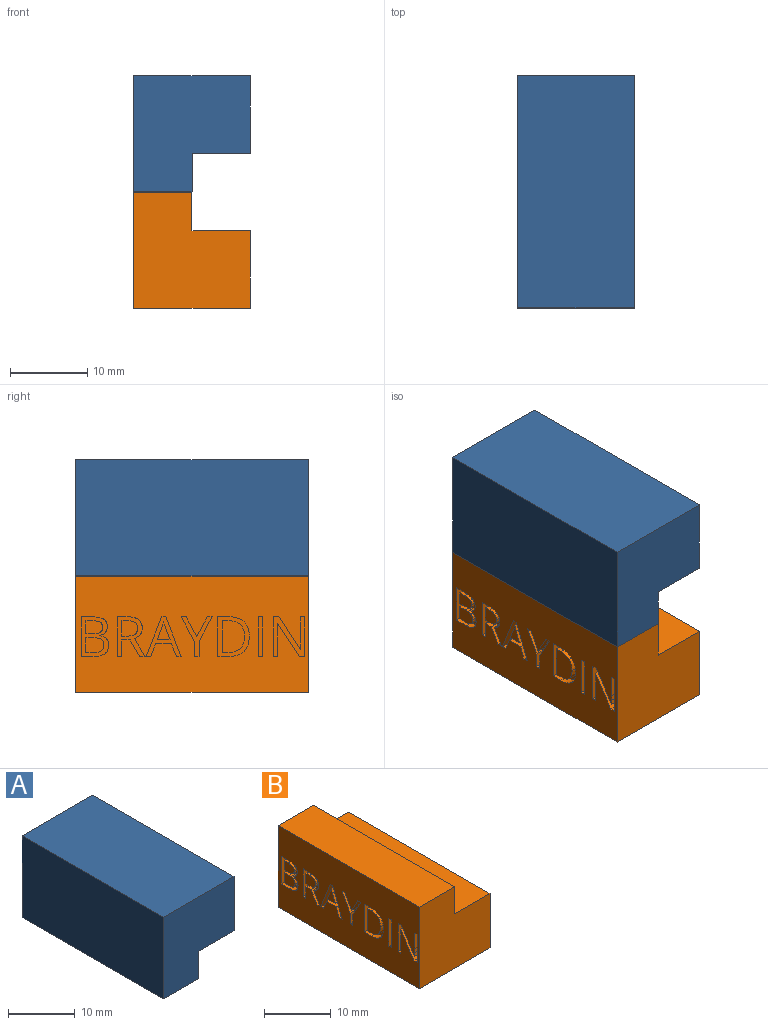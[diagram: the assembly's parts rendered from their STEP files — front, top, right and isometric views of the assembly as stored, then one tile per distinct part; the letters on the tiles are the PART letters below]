
ASSEMBLY  parts=2 mates=1
PART A: 8 faces, bbox 15x30x15 mm
  f0: plane 30x15mm, normal (0,0,1), area 450mm2, adj f1,f2,f3,f6
  f1: plane 30x15mm, normal (-1,0,0), area 450mm2, adj f0,f2,f3,f5
  f2: plane 15x15mm, normal (0,-1,0), area 187.5mm2, adj f0,f1,f4,f5,f6,f7
  f3: plane 15x15mm, normal (0,1,0), area 187.5mm2, adj f0,f1,f4,f5,f6,f7
  f4: plane 30x5mm, normal (1,0,0), area 150mm2, adj f2,f3,f5,f7
  f5: plane 30x7.5mm, normal (0,0,-1), area 225mm2, adj f1,f2,f3,f4
  f6: plane 30x10mm, normal (1,0,0), area 300mm2, adj f0,f2,f3,f7
  f7: plane 30x7.5mm, normal (0,0,-1), area 225mm2, adj f2,f3,f4,f6
PART B: 118 faces, bbox 15x30x15 mm
  f0: plane 30x15mm, normal (-1,0,0), area 378.6mm2, adj f1,f3,f4,f7,f8,f9,f10,f11
  f1: plane 15x15mm, normal (0,-1,0), area 187.5mm2, adj f0,f2,f4,f5,f6,f7
  f2: plane 30x5mm, normal (1,0,0), area 150mm2, adj f1,f3,f6,f7
  f3: plane 15x15mm, normal (0,1,0), area 187.5mm2, adj f0,f2,f4,f5,f6,f7
  f4: plane 30x15mm, normal (0,0,-1), area 450mm2, adj f0,f1,f3,f5
  f5: plane 30x10mm, normal (1,0,0), area 300mm2, adj f1,f3,f4,f6
  f6: plane 30x7.5mm, normal (0,0,1), area 225mm2, adj f1,f2,f3,f5
  f7: plane 30x7.5mm, normal (0,0,1), area 225mm2, adj f0,f1,f2,f3
  f8: plane 2.56x1.36mm, normal (0,-0.88,-0.47), area 2.9mm2, adj f0,f9,f16,f17
  f9: plane 2.56x1.35mm, normal (0,0.88,-0.47), area 2.9mm2, adj f0,f8,f10,f17
  f10: plane 1x0.65mm, normal (0,0,-1), area 0.7mm2, adj f0,f9,f11,f17
  f11: plane 3.16x1.7mm, normal (0,-0.88,0.47), area 3.6mm2, adj f0,f10,f12,f17
  f12: plane 1.96x1mm, normal (0,-1,0), area 2mm2, adj f0,f11,f13,f17
  f13: plane 1x0.6mm, normal (0,0,1), area 0.6mm2, adj f0,f12,f14,f17
  f14: plane 1.98x1mm, normal (0,1,0), area 2mm2, adj f0,f13,f15,f17
  f15: plane 3.13x1.71mm, normal (0,0.88,0.48), area 3.6mm2, adj f0,f14,f16,f17
  f16: plane 1x0.64mm, normal (0,0,-1), area 0.6mm2, adj f0,f8,f15,f17
  f17: plane 5.11x4.01mm, normal (-1,0,0), area 5mm2, adj f8,f9,f10,f11,f12,f13,f14,f15
  f18: plane 1.91x1mm, normal (0,1,0), area 1.9mm2, adj f19,f42,f43,f114
  f19: plane 1.02x1mm, normal (0,0,1), area 1mm2, adj f18,f20,f43,f114
  f20: extruded ~1x0.97mm, area 1mm2, adj f19,f21,f43,f114
  f21: extruded ~1x0.7mm, area 0.8mm2, adj f20,f22,f43,f114
  f22: extruded ~1x0.75mm, area 0.8mm2, adj f21,f23,f43,f114
  f23: extruded ~1x0.93mm, area 1mm2, adj f22,f42,f43,f114
  f24: plane 1x0.98mm, normal (0,0,-1), area 1mm2, adj f25,f40,f43,f44
  f25: plane 1.67x1mm, normal (0,1,0), area 1.7mm2, adj f24,f26,f43,f44
  f26: plane 1x0.88mm, normal (0,0,1), area 0.9mm2, adj f25,f27,f43,f44
  f27: extruded ~1x0.98mm, area 1mm2, adj f26,f28,f43,f44
  f28: extruded ~1x0.62mm, area 0.7mm2, adj f27,f29,f43,f44
  f29: extruded ~1x0.67mm, area 0.8mm2, adj f28,f40,f43,f44
  f30: plane 1.45x1mm, normal (0,0,-1), area 1.4mm2, adj f0,f31,f41,f43
  f31: plane 5.11x1mm, normal (0,-1,0), area 5.1mm2, adj f0,f30,f32,f43
  f32: plane 1.78x1mm, normal (0,0,1), area 1.8mm2, adj f0,f31,f33,f43
  f33: extruded ~1.3x1mm, area 1.4mm2, adj f0,f32,f34,f43
  f34: extruded ~1.07x1mm, area 1.2mm2, adj f0,f33,f35,f43
  f35: extruded ~1.22x1.17mm, area 1.9mm2, adj f0,f34,f36,f43
  f36: plane 1x0.03mm, normal (0,1,0), area 0mm2, adj f0,f35,f37,f43
  f37: extruded ~1x0.74mm, area 0.9mm2, adj f0,f36,f38,f43
  f38: extruded ~1x0.75mm, area 0.8mm2, adj f0,f37,f39,f43
  f39: extruded ~1x0.96mm, area 1.1mm2, adj f0,f38,f41,f43
  f40: extruded ~1x0.91mm, area 0.9mm2, adj f24,f29,f43,f44
  f41: extruded ~1.47x1mm, area 1.5mm2, adj f0,f30,f39,f43
  f42: plane 1.07x1mm, normal (0,0,-1), area 1.1mm2, adj f18,f23,f43,f114
  f43: plane 5.11x3.54mm, normal (-1,0,0), area 8.9mm2, adj f18,f19,f20,f21,f22,f23,f24,f25
  f44: plane 2.16x1.67mm, normal (-1,0,0), area 3.3mm2, adj f24,f25,f26,f27,f28,f29,f40
  f45: extruded ~1.51x1mm, area 1.6mm2, adj f46,f58,f59,f115
  f46: extruded ~1.55x1mm, area 1.7mm2, adj f45,f47,f59,f115
  f47: extruded ~1.6x1mm, area 1.7mm2, adj f46,f48,f59,f115
  f48: plane 1x0.72mm, normal (0,0,-1), area 0.7mm2, adj f47,f49,f59,f115
  f49: plane 4.09x1mm, normal (0,1,0), area 4.1mm2, adj f48,f50,f59,f115
  f50: plane 1x0.86mm, normal (0,0,1), area 0.9mm2, adj f49,f58,f59,f115
  f51: extruded ~1.94x1mm, area 2.1mm2, adj f0,f52,f57,f59
  f52: extruded ~1.85x1mm, area 2mm2, adj f0,f51,f53,f59
  f53: extruded ~1.85x1mm, area 2mm2, adj f0,f52,f54,f59
  f54: plane 1.57x1mm, normal (0,0,-1), area 1.6mm2, adj f0,f53,f55,f59
  f55: plane 5.11x1mm, normal (0,-1,0), area 5.1mm2, adj f0,f54,f56,f59
  f56: plane 1.42x1mm, normal (0,0,1), area 1.4mm2, adj f0,f55,f57,f59
  f57: extruded ~1.98x1mm, area 2.1mm2, adj f0,f51,f56,f59
  f58: extruded ~1.49x1mm, area 1.6mm2, adj f45,f50,f59,f115
  f59: plane 5.11x4.08mm, normal (-1,0,0), area 8.3mm2, adj f45,f46,f47,f48,f49,f50,f51,f52
  f60: plane 1.59x1mm, normal (0,-0.94,0.35), area 1.7mm2, adj f61,f72,f73,f116
  f61: plane 1.65x1mm, normal (0,0,-1), area 1.7mm2, adj f60,f62,f73,f116
  f62: plane 1.59x1mm, normal (0,0.94,0.35), area 1.7mm2, adj f61,f63,f73,f116
  f63: extruded ~1x0.74mm, area 0.8mm2, adj f62,f72,f73,f116
  f64: plane 1.63x1mm, normal (0,-0.93,0.36), area 1.7mm2, adj f0,f65,f71,f73
  f65: plane 1x0.62mm, normal (0,0,1), area 0.6mm2, adj f0,f64,f66,f73
  f66: plane 5.14x2.01mm, normal (0,0.93,-0.36), area 5.5mm2, adj f0,f65,f67,f73
  f67: plane 1x0.5mm, normal (0,0,-1), area 0.5mm2, adj f0,f66,f68,f73
  f68: plane 5.14x2.02mm, normal (0,-0.93,-0.37), area 5.5mm2, adj f0,f67,f69,f73
  f69: plane 1x0.6mm, normal (0,0,1), area 0.6mm2, adj f0,f68,f70,f73
  f70: plane 1.63x1mm, normal (0,0.93,0.36), area 1.7mm2, adj f0,f69,f71,f73
  f71: plane 2.05x1mm, normal (0,0,1), area 2mm2, adj f0,f64,f70,f73
  f72: extruded ~1x0.74mm, area 0.8mm2, adj f60,f63,f73,f116
  f73: plane 5.14x4.53mm, normal (-1,0,0), area 6.7mm2, adj f60,f61,f62,f63,f64,f65,f66,f67
  f74: plane 1x0.82mm, normal (0,0,-1), area 0.8mm2, adj f75,f91,f92,f117
  f75: plane 1.96x1mm, normal (0,1,0), area 2mm2, adj f74,f76,f92,f117
  f76: plane 1x0.77mm, normal (0,0,1), area 0.8mm2, adj f75,f77,f92,f117
  f77: extruded ~1x0.96mm, area 1mm2, adj f76,f78,f92,f117
  f78: extruded ~1x0.73mm, area 0.8mm2, adj f77,f79,f92,f117
  f79: extruded ~1x0.75mm, area 0.8mm2, adj f78,f91,f92,f117
  f80: plane 2.13x1mm, normal (0,1,0), area 2.1mm2, adj f0,f81,f90,f92
  f81: plane 1.07x1mm, normal (0,0,1), area 1.1mm2, adj f0,f80,f82,f92
  f82: plane 2.13x1.24mm, normal (0,-0.86,0.5), area 2.5mm2, adj f0,f81,f83,f92
  f83: plane 1x0.7mm, normal (0,0,1), area 0.7mm2, adj f0,f82,f84,f92
  f84: plane 2.3x1.39mm, normal (0,0.86,-0.52), area 2.7mm2, adj f0,f83,f85,f92
  f85: extruded ~1.37x1.03mm, area 1.8mm2, adj f0,f84,f86,f92
  f86: extruded ~1.08x1mm, area 1.2mm2, adj f0,f85,f87,f92
  f87: extruded ~1.39x1mm, area 1.5mm2, adj f0,f86,f88,f92
  f88: plane 1.4x1mm, normal (0,0,-1), area 1.4mm2, adj f0,f87,f89,f92
  f89: plane 5.11x1mm, normal (0,-1,0), area 5.1mm2, adj f0,f88,f90,f92
  f90: plane 1x0.59mm, normal (0,0,1), area 0.6mm2, adj f0,f80,f89,f92
  f91: extruded ~1x0.92mm, area 1mm2, adj f74,f79,f92,f117
  f92: plane 5.11x3.6mm, normal (-1,0,0), area 7.8mm2, adj f74,f75,f76,f77,f78,f79,f80,f81
  f93: plane 1x0.68mm, normal (0,0,1), area 0.7mm2, adj f0,f94,f107,f108
  f94: plane 5.11x1mm, normal (0,1,0), area 5.1mm2, adj f0,f93,f95,f108
  f95: plane 1x0.56mm, normal (0,0,-1), area 0.6mm2, adj f0,f94,f96,f108
  f96: plane 2.94x1mm, normal (0,-1,0), area 2.9mm2, adj f0,f95,f97,f108
  f97: extruded ~1x0.73mm, area 0.7mm2, adj f0,f96,f98,f108
  f98: extruded ~1x0.61mm, area 0.6mm2, adj f0,f97,f99,f108
  f99: plane 1x0.03mm, normal (0,0,-1), area 0mm2, adj f0,f98,f100,f108
  f100: plane 4.28x2.79mm, normal (0,0.84,-0.55), area 5.1mm2, adj f0,f99,f101,f108
  f101: plane 1x0.67mm, normal (0,0,-1), area 0.7mm2, adj f0,f100,f102,f108
  f102: plane 5.11x1mm, normal (0,-1,0), area 5.1mm2, adj f0,f101,f103,f108
  f103: plane 1x0.55mm, normal (0,0,1), area 0.5mm2, adj f0,f102,f104,f108
  f104: plane 2.91x1mm, normal (0,1,0), area 2.9mm2, adj f0,f103,f105,f108
  f105: extruded ~1.38x1mm, area 1.4mm2, adj f0,f104,f106,f108
  f106: plane 1x0.03mm, normal (0,0,1), area 0mm2, adj f0,f105,f107,f108
  f107: plane 4.29x2.8mm, normal (0,-0.84,0.55), area 5.1mm2, adj f0,f93,f106,f108
  f108: plane 5.11x4mm, normal (-1,0,0), area 8.6mm2, adj f93,f94,f95,f96,f97,f98,f99,f100
  f109: plane 5.11x1mm, normal (0,-1,0), area 5.1mm2, adj f0,f110,f112,f113
  f110: plane 1x0.59mm, normal (0,0,1), area 0.6mm2, adj f0,f109,f111,f113
  f111: plane 5.11x1mm, normal (0,1,0), area 5.1mm2, adj f0,f110,f112,f113
  f112: plane 1x0.59mm, normal (0,0,-1), area 0.6mm2, adj f0,f109,f111,f113
  f113: plane 5.11x0.59mm, normal (-1,0,0), area 3mm2, adj f109,f110,f111,f112
  f114: plane 2.31x1.91mm, normal (-1,0,0), area 4mm2, adj f18,f19,f20,f21,f22,f23,f42
  f115: plane 4.09x2.86mm, normal (-1,0,0), area 10.3mm2, adj f45,f46,f47,f48,f49,f50,f58
  f116: plane 2.32x1.65mm, normal (-1,0,0), area 1.8mm2, adj f60,f61,f62,f63,f72
  f117: plane 2.03x1.96mm, normal (-1,0,0), area 3.6mm2, adj f74,f75,f76,f77,f78,f79,f91
PLACE A t=(-0.73,-1.91,-6.2)mm
PLACE B t=(9.64,-1.91,-13.23)mm
MATE parallel A.f5 <-> B.f7  axis (0,0,-1) through (-46.66,-16.91,19.3)mm
